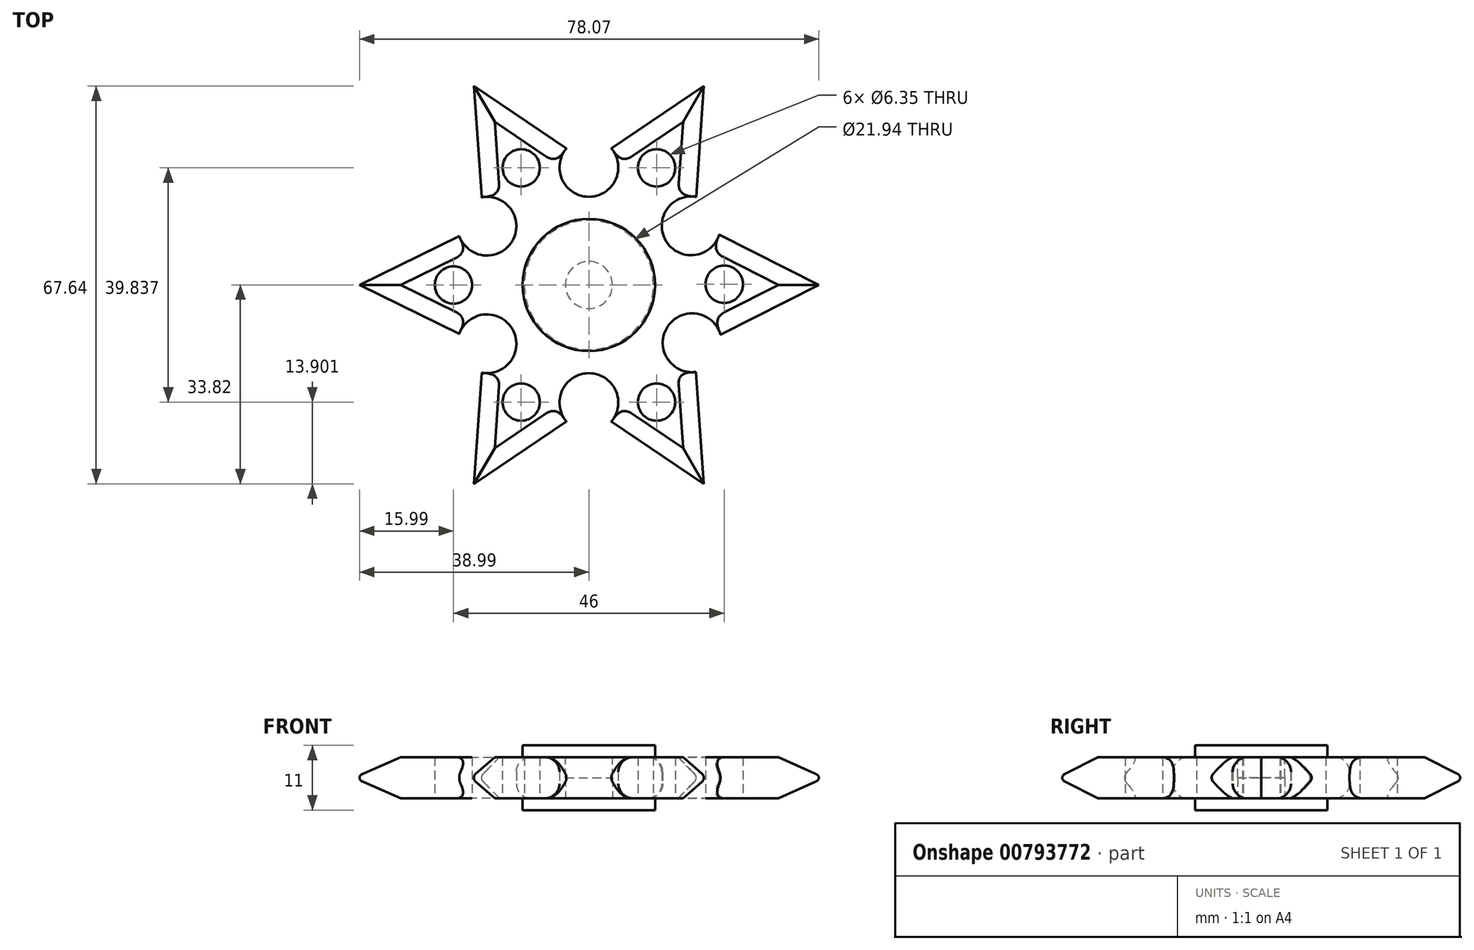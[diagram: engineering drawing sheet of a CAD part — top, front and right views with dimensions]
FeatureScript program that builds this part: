
annotation { "Feature Type Name" : "Feature", "Feature Type Description" : "" }
export const myFeature = defineFeature(function(context is Context, id is Id, definition is map)
    precondition{}
    {
        {
            var Q0;
            Q0=qCreatedBy(makeId("Top.planeOp"),FACE);
            var sketch = newSketch(context, id + "F0", { "sketchPlane" : qUnion([Q0])});
            skCircle(sketch, "E0", {"center": v(0, 0) * mm, "radius": 10.97 * mm});
            skCircle(sketch, "E1.cCircle", {"center": v(0, 0) * mm, "radius": 10.97 * mm, "construction": true});
            skLineSegment(sketch, "E1.0", {"start": v(0, -10.97) * mm, "end": v(-9.5, -5.48) * mm});
            skLineSegment(sketch, "E1.1", {"start": v(-9.5, -5.49) * mm, "end": v(-9.5, 5.49) * mm});
            skLineSegment(sketch, "E1.2", {"start": v(-9.5, 5.49) * mm, "end": v(0, 10.97) * mm});
            skLineSegment(sketch, "E1.3", {"start": v(0, 10.97) * mm, "end": v(9.5, 5.48) * mm});
            skLineSegment(sketch, "E1.4", {"start": v(9.5, 5.49) * mm, "end": v(9.5, -5.49) * mm});
            skLineSegment(sketch, "E1.5", {"start": v(9.5, -5.49) * mm, "end": v(0, -10.97) * mm});
            skLineSegment(sketch, "E2", {"start": v(-18.61, 14.83) * mm, "end": v(-20, 34.64) * mm});
            skLineSegment(sketch, "E3", {"start": v(-20, 34.64) * mm, "end": v(-3.54, 23.54) * mm});
            skLineSegment(sketch, "E4", {"start": v(-39.94, 0) * mm, "end": v(-22.15, 8.7) * mm});
            skLineSegment(sketch, "E5", {"start": v(3.54, 23.54) * mm, "end": v(20, 34.64) * mm});
            skLineSegment(sketch, "E6", {"start": v(-39.94, 0) * mm, "end": v(-22.15, -8.7) * mm});
            skLineSegment(sketch, "E7", {"start": v(20, 34.64) * mm, "end": v(18.63, 14.9) * mm});
            skLineSegment(sketch, "E8", {"start": v(-20, -34.64) * mm, "end": v(-18.61, -14.83) * mm});
            skLineSegment(sketch, "E9", {"start": v(-20, -34.64) * mm, "end": v(-3.54, -23.54) * mm});
            skLineSegment(sketch, "E10", {"start": v(3.54, -23.54) * mm, "end": v(20, -34.64) * mm});
            skLineSegment(sketch, "E11", {"start": v(22.26, 8.97) * mm, "end": v(40, 0) * mm});
            skLineSegment(sketch, "E12", {"start": v(20, -34.64) * mm, "end": v(18.59, -14.73) * mm});
            skLineSegment(sketch, "E13", {"start": v(40, 0) * mm, "end": v(22.46, -8.84) * mm});
            skArc(sketch, "E14", {"start": v(-22.15, 8.7) * mm, "mid": v(-13, 7.5) * mm, "end": v(-18.61, 14.83) * mm});
            skArc(sketch, "E15", {"start": v(-3.54, 23.54) * mm, "mid": v(0, 15) * mm, "end": v(3.54, 23.54) * mm});
            skArc(sketch, "E16", {"start": v(-18.61, -14.83) * mm, "mid": v(-13, -7.5) * mm, "end": v(-22.15, -8.7) * mm});
            skArc(sketch, "E17", {"start": v(3.54, -23.54) * mm, "mid": v(0, -15) * mm, "end": v(-3.54, -23.54) * mm});
            skArc(sketch, "E18", {"start": v(22.46, -8.84) * mm, "mid": v(13.38, -7.09) * mm, "end": v(18.59, -14.73) * mm});
            skArc(sketch, "E19", {"start": v(18.63, 14.9) * mm, "mid": v(13.11, 7.45) * mm, "end": v(22.26, 8.97) * mm});
            skCircle(sketch, "E20", {"center": v(-11.5, 19.92) * mm, "radius": 3.17 * mm});
            skCircle(sketch, "E21", {"center": v(-23, 0) * mm, "radius": 3.17 * mm});
            skCircle(sketch, "E22", {"center": v(-11.5, -19.92) * mm, "radius": 3.17 * mm});
            skCircle(sketch, "E23", {"center": v(11.5, -19.92) * mm, "radius": 3.17 * mm});
            skCircle(sketch, "E24", {"center": v(23, 0.12) * mm, "radius": 3.17 * mm});
            skCircle(sketch, "E25", {"center": v(11.5, 19.92) * mm, "radius": 3.17 * mm});
            skLineSegment(sketch, "E26", {"start": v(-23, 0) * mm, "end": v(0, 0) * mm});
            skLineSegment(sketch, "E27", {"start": v(0, 0) * mm, "end": v(-11.5, 19.92) * mm});
            skLineSegment(sketch, "E28", {"start": v(0, 0) * mm, "end": v(11.5, 19.92) * mm});
            skLineSegment(sketch, "E29", {"start": v(0, 0) * mm, "end": v(23, 0.12) * mm});
            skLineSegment(sketch, "E30", {"start": v(0, 0) * mm, "end": v(11.5, -19.92) * mm});
            skLineSegment(sketch, "E31", {"start": v(0, 0) * mm, "end": v(-11.5, -19.92) * mm});
            skSolve(sketch);
        }
        {
            var Q0;
            Q0 = qSketchRegion(id + "F0", true);
            extrude(context, id + "F1", {"entities" : qUnion([Q0]), "endBound" : BoundingType.SYMMETRIC, "depth" : 7 * mm, "offsetDistance" : 25 * mm});
        }
        {
            var Q0;
            Q0=makeQuery(id+"F1.opExtrude","CAP_EDGE",EDGE,{"disambiguationData":[OSD([sQuery(id+"F0.wireOp",EDGE,"E4")])],"isStart":true});
            var Q1;
            Q1=makeQuery(id+"F1.opExtrude","CAP_EDGE",EDGE,{"disambiguationData":[OSD([sQuery(id+"F0.wireOp",EDGE,"E6")])],"isStart":true});
            var Q2;
            Q2=makeQuery(id+"F1.opExtrude","CAP_EDGE",EDGE,{"disambiguationData":[OSD([sQuery(id+"F0.wireOp",EDGE,"E2")])],"isStart":true});
            var Q3;
            Q3=makeQuery(id+"F1.opExtrude","CAP_EDGE",EDGE,{"disambiguationData":[OSD([sQuery(id+"F0.wireOp",EDGE,"E3")])],"isStart":true});
            var Q4;
            Q4=makeQuery(id+"F1.opExtrude","CAP_EDGE",EDGE,{"disambiguationData":[OSD([sQuery(id+"F0.wireOp",EDGE,"E5")])],"isStart":true});
            var Q5;
            Q5=makeQuery(id+"F1.opExtrude","CAP_EDGE",EDGE,{"disambiguationData":[OSD([sQuery(id+"F0.wireOp",EDGE,"E7")])],"isStart":true});
            var Q6;
            Q6=makeQuery(id+"F1.opExtrude","CAP_EDGE",EDGE,{"disambiguationData":[OSD([sQuery(id+"F0.wireOp",EDGE,"E11")])],"isStart":true});
            var Q7;
            Q7=makeQuery(id+"F1.opExtrude","CAP_EDGE",EDGE,{"disambiguationData":[OSD([sQuery(id+"F0.wireOp",EDGE,"E13")])],"isStart":true});
            var Q8;
            Q8=makeQuery(id+"F1.opExtrude","CAP_EDGE",EDGE,{"disambiguationData":[OSD([sQuery(id+"F0.wireOp",EDGE,"E8")])],"isStart":true});
            var Q9;
            Q9=makeQuery(id+"F1.opExtrude","CAP_EDGE",EDGE,{"disambiguationData":[OSD([sQuery(id+"F0.wireOp",EDGE,"E9")])],"isStart":true});
            var Q10;
            Q10=makeQuery(id+"F1.opExtrude","CAP_EDGE",EDGE,{"disambiguationData":[OSD([sQuery(id+"F0.wireOp",EDGE,"E10")])],"isStart":true});
            var Q11;
            Q11=makeQuery(id+"F1.opExtrude","CAP_EDGE",EDGE,{"disambiguationData":[OSD([sQuery(id+"F0.wireOp",EDGE,"E12")])],"isStart":true});
            var Q12;
            Q12=makeQuery(id+"F1.opExtrude","CAP_EDGE",EDGE,{"disambiguationData":[OSD([sQuery(id+"F0.wireOp",EDGE,"E3")])],"isStart":false});
            var Q13;
            Q13=makeQuery(id+"F1.opExtrude","CAP_EDGE",EDGE,{"disambiguationData":[OSD([sQuery(id+"F0.wireOp",EDGE,"E2")])],"isStart":false});
            var Q14;
            Q14=makeQuery(id+"F1.opExtrude","CAP_EDGE",EDGE,{"disambiguationData":[OSD([sQuery(id+"F0.wireOp",EDGE,"E5")])],"isStart":false});
            var Q15;
            Q15=makeQuery(id+"F1.opExtrude","CAP_EDGE",EDGE,{"disambiguationData":[OSD([sQuery(id+"F0.wireOp",EDGE,"E7")])],"isStart":false});
            var Q16;
            Q16=makeQuery(id+"F1.opExtrude","CAP_EDGE",EDGE,{"disambiguationData":[OSD([sQuery(id+"F0.wireOp",EDGE,"E11")])],"isStart":false});
            var Q17;
            Q17=makeQuery(id+"F1.opExtrude","CAP_EDGE",EDGE,{"disambiguationData":[OSD([sQuery(id+"F0.wireOp",EDGE,"E13")])],"isStart":false});
            var Q18;
            Q18=makeQuery(id+"F1.opExtrude","CAP_EDGE",EDGE,{"disambiguationData":[OSD([sQuery(id+"F0.wireOp",EDGE,"E6")])],"isStart":false});
            var Q19;
            Q19=makeQuery(id+"F1.opExtrude","CAP_EDGE",EDGE,{"disambiguationData":[OSD([sQuery(id+"F0.wireOp",EDGE,"E4")])],"isStart":false});
            var Q20;
            Q20=makeQuery(id+"F1.opExtrude","CAP_EDGE",EDGE,{"disambiguationData":[OSD([sQuery(id+"F0.wireOp",EDGE,"E8")])],"isStart":false});
            var Q21;
            Q21=makeQuery(id+"F1.opExtrude","CAP_EDGE",EDGE,{"disambiguationData":[OSD([sQuery(id+"F0.wireOp",EDGE,"E9")])],"isStart":false});
            var Q22;
            Q22=makeQuery(id+"F1.opExtrude","CAP_EDGE",EDGE,{"disambiguationData":[OSD([sQuery(id+"F0.wireOp",EDGE,"E10")])],"isStart":false});
            var Q23;
            Q23=makeQuery(id+"F1.opExtrude","CAP_EDGE",EDGE,{"disambiguationData":[OSD([sQuery(id+"F0.wireOp",EDGE,"E12")])],"isStart":false});
            chamfer(context, id + "F2", {"entities" : qUnion([Q0, Q1, Q2, Q3, Q4, Q5, Q6, Q7, Q8, Q9, Q10, Q11, Q12, Q13, Q14, Q15, Q16, Q17, Q18, Q19, Q20, Q21, Q22, Q23]), "width" : 3.5 * mm, "tangentPropagation" : true});
        }
        {
            var Q0;
            Q0=makeQuery(id+"F1.opExtrude","CAP_EDGE",EDGE,{"disambiguationData":[OSD([sQuery(id+"F0.wireOp",EDGE,"E16")])],"isStart":true});
            var Q1;
            Q1=makeQuery(id+"F1.opExtrude","CAP_EDGE",EDGE,{"disambiguationData":[OSD([sQuery(id+"F0.wireOp",EDGE,"E16")])],"isStart":false});
            var Q2;
            Q2=makeQuery(id+"F1.opExtrude","CAP_EDGE",EDGE,{"disambiguationData":[OSD([sQuery(id+"F0.wireOp",EDGE,"E14")])],"isStart":true});
            var Q3;
            Q3=makeQuery(id+"F1.opExtrude","CAP_EDGE",EDGE,{"disambiguationData":[OSD([sQuery(id+"F0.wireOp",EDGE,"E14")])],"isStart":false});
            var Q4;
            Q4=makeQuery(id+"F1.opExtrude","CAP_EDGE",EDGE,{"disambiguationData":[OSD([sQuery(id+"F0.wireOp",EDGE,"E15")])],"isStart":true});
            var Q5;
            Q5=makeQuery(id+"F1.opExtrude","CAP_EDGE",EDGE,{"disambiguationData":[OSD([sQuery(id+"F0.wireOp",EDGE,"E19")])],"isStart":true});
            var Q6;
            Q6=makeQuery(id+"F1.opExtrude","CAP_EDGE",EDGE,{"disambiguationData":[OSD([sQuery(id+"F0.wireOp",EDGE,"E18")])],"isStart":true});
            var Q7;
            Q7=makeQuery(id+"F1.opExtrude","CAP_EDGE",EDGE,{"disambiguationData":[OSD([sQuery(id+"F0.wireOp",EDGE,"E17")])],"isStart":true});
            var Q8;
            Q8=makeQuery(id+"F1.opExtrude","CAP_EDGE",EDGE,{"disambiguationData":[OSD([sQuery(id+"F0.wireOp",EDGE,"E19")])],"isStart":false});
            var Q9;
            Q9=makeQuery(id+"F1.opExtrude","CAP_EDGE",EDGE,{"disambiguationData":[OSD([sQuery(id+"F0.wireOp",EDGE,"E18")])],"isStart":false});
            var Q10;
            Q10=makeQuery(id+"F1.opExtrude","CAP_EDGE",EDGE,{"disambiguationData":[OSD([sQuery(id+"F0.wireOp",EDGE,"E17")])],"isStart":false});
            var Q11;
            Q11=makeQuery(id+"F1.opExtrude","CAP_EDGE",EDGE,{"disambiguationData":[OSD([sQuery(id+"F0.wireOp",EDGE,"E15")])],"isStart":false});
            fillet(context, id + "F3", {"entities" : qUnion([Q0, Q1, Q2, Q3, Q4, Q5, Q6, Q7, Q8, Q9, Q10, Q11]), "radius" : 2.5 * mm, "tangentPropagation" : true, "allowEdgeOverflow" : false});
        }
        {
            var Q0;
            Q0=makeQuery(id+"F1.opExtrude","CAP_FACE",FACE,{"disambiguationData":[OSD([sQuery(id+"F0.wireOp",EDGE,"E0"),sQuery(id+"F0.wireOp",EDGE,"E2"),sQuery(id+"F0.wireOp",EDGE,"E3"),sQuery(id+"F0.wireOp",EDGE,"E4"),sQuery(id+"F0.wireOp",EDGE,"E5"),sQuery(id+"F0.wireOp",EDGE,"E6"),sQuery(id+"F0.wireOp",EDGE,"E7"),sQuery(id+"F0.wireOp",EDGE,"E8"),sQuery(id+"F0.wireOp",EDGE,"E9"),sQuery(id+"F0.wireOp",EDGE,"E10"),sQuery(id+"F0.wireOp",EDGE,"E11"),sQuery(id+"F0.wireOp",EDGE,"E12"),sQuery(id+"F0.wireOp",EDGE,"E13"),sQuery(id+"F0.wireOp",EDGE,"E14"),sQuery(id+"F0.wireOp",EDGE,"E15"),sQuery(id+"F0.wireOp",EDGE,"E16"),sQuery(id+"F0.wireOp",EDGE,"E17"),sQuery(id+"F0.wireOp",EDGE,"E18"),sQuery(id+"F0.wireOp",EDGE,"E19")])],"isStart":true});
            var sketch = newSketch(context, id + "F4", { "sketchPlane" : qUnion([Q0])});
            skCircle(sketch, "E32", {"center": v(0, 0) * mm, "radius": 4 * mm});
            skCircle(sketch, "E33", {"center": v(0, 0) * mm, "radius": 11.25 * mm});
            skSolve(sketch);
        }
        {
            var Q0;
            Q0 = qSketchRegion(id + "F4", true);
            var Q1;
            Q1=makeQuery(id+"F4.imprint","IMPRINT",FACE,{"disambiguationData":[TD([[makeQuery(id+"F4.imprint","IMPRINT",EDGE,{"derivedFrom":sQuery(id+"F4.wireOp",EDGE,"E32")}),1.0]])]});
            extrude(context, id + "F5", {"entities" : qUnion([Q0, Q1]), "depth" : 2 * mm, "offsetDistance" : 25 * mm});
        }
        {
            var Q0;
            Q0=makeQuery(id+"F4.imprint","IMPRINT",FACE,{"disambiguationData":[TD([[makeQuery(id+"F4.imprint","IMPRINT",EDGE,{"derivedFrom":sQuery(id+"F4.wireOp",EDGE,"E32")}),1.0]])]});
            extrude(context, id + "F6", {"entities" : qUnion([Q0]), "operationType" : NewBodyOperationType.ADD, "oppositeDirection" : true, "depth" : 3.5 * mm, "offsetDistance" : 25 * mm});
        }
        {
            var Q0;
            {var subQ0=sQuery(id+"F0.wireOp",EDGE,"E9");Q0=makeQuery(id+"F2.opChamfer","BLEND_EDGE",EDGE,{"blendedFrom":[makeQuery(id+"F1.opExtrude","CAP_EDGE",EDGE,{"disambiguationData":[OSD([subQ0])],"isStart":true}),makeQuery(id+"F1.opExtrude","CAP_EDGE",EDGE,{"disambiguationData":[OSD([subQ0])],"isStart":false})],"blendedInto":[]});}
            var Q1;
            {var subQ0=sQuery(id+"F0.wireOp",EDGE,"E10");Q1=makeQuery(id+"F2.opChamfer","BLEND_EDGE",EDGE,{"blendedFrom":[makeQuery(id+"F1.opExtrude","CAP_EDGE",EDGE,{"disambiguationData":[OSD([subQ0])],"isStart":true}),makeQuery(id+"F1.opExtrude","CAP_EDGE",EDGE,{"disambiguationData":[OSD([subQ0])],"isStart":false})],"blendedInto":[]});}
            var Q2;
            {var subQ0=sQuery(id+"F0.wireOp",EDGE,"E12");Q2=makeQuery(id+"F2.opChamfer","BLEND_EDGE",EDGE,{"blendedFrom":[makeQuery(id+"F1.opExtrude","CAP_EDGE",EDGE,{"disambiguationData":[OSD([subQ0])],"isStart":true}),makeQuery(id+"F1.opExtrude","CAP_EDGE",EDGE,{"disambiguationData":[OSD([subQ0])],"isStart":false})],"blendedInto":[]});}
            var Q3;
            {var subQ0=sQuery(id+"F0.wireOp",EDGE,"E13");Q3=makeQuery(id+"F2.opChamfer","BLEND_EDGE",EDGE,{"blendedFrom":[makeQuery(id+"F1.opExtrude","CAP_EDGE",EDGE,{"disambiguationData":[OSD([subQ0])],"isStart":true}),makeQuery(id+"F1.opExtrude","CAP_EDGE",EDGE,{"disambiguationData":[OSD([subQ0])],"isStart":false})],"blendedInto":[]});}
            var Q4;
            {var subQ0=sQuery(id+"F0.wireOp",EDGE,"E11");Q4=makeQuery(id+"F2.opChamfer","BLEND_EDGE",EDGE,{"blendedFrom":[makeQuery(id+"F1.opExtrude","CAP_EDGE",EDGE,{"disambiguationData":[OSD([subQ0])],"isStart":true}),makeQuery(id+"F1.opExtrude","CAP_EDGE",EDGE,{"disambiguationData":[OSD([subQ0])],"isStart":false})],"blendedInto":[]});}
            var Q5;
            {var subQ0=sQuery(id+"F0.wireOp",EDGE,"E7");Q5=makeQuery(id+"F2.opChamfer","BLEND_EDGE",EDGE,{"blendedFrom":[makeQuery(id+"F1.opExtrude","CAP_EDGE",EDGE,{"disambiguationData":[OSD([subQ0])],"isStart":true}),makeQuery(id+"F1.opExtrude","CAP_EDGE",EDGE,{"disambiguationData":[OSD([subQ0])],"isStart":false})],"blendedInto":[]});}
            var Q6;
            {var subQ0=sQuery(id+"F0.wireOp",EDGE,"E5");Q6=makeQuery(id+"F2.opChamfer","BLEND_EDGE",EDGE,{"blendedFrom":[makeQuery(id+"F1.opExtrude","CAP_EDGE",EDGE,{"disambiguationData":[OSD([subQ0])],"isStart":true}),makeQuery(id+"F1.opExtrude","CAP_EDGE",EDGE,{"disambiguationData":[OSD([subQ0])],"isStart":false})],"blendedInto":[]});}
            var Q7;
            {var subQ0=sQuery(id+"F0.wireOp",EDGE,"E3");Q7=makeQuery(id+"F2.opChamfer","BLEND_EDGE",EDGE,{"blendedFrom":[makeQuery(id+"F1.opExtrude","CAP_EDGE",EDGE,{"disambiguationData":[OSD([subQ0])],"isStart":true}),makeQuery(id+"F1.opExtrude","CAP_EDGE",EDGE,{"disambiguationData":[OSD([subQ0])],"isStart":false})],"blendedInto":[]});}
            var Q8;
            {var subQ0=sQuery(id+"F0.wireOp",EDGE,"E2");Q8=makeQuery(id+"F2.opChamfer","BLEND_EDGE",EDGE,{"blendedFrom":[makeQuery(id+"F1.opExtrude","CAP_EDGE",EDGE,{"disambiguationData":[OSD([subQ0])],"isStart":true}),makeQuery(id+"F1.opExtrude","CAP_EDGE",EDGE,{"disambiguationData":[OSD([subQ0])],"isStart":false})],"blendedInto":[]});}
            var Q9;
            {var subQ0=sQuery(id+"F0.wireOp",EDGE,"E4");Q9=makeQuery(id+"F2.opChamfer","BLEND_EDGE",EDGE,{"blendedFrom":[makeQuery(id+"F1.opExtrude","CAP_EDGE",EDGE,{"disambiguationData":[OSD([subQ0])],"isStart":true}),makeQuery(id+"F1.opExtrude","CAP_EDGE",EDGE,{"disambiguationData":[OSD([subQ0])],"isStart":false})],"blendedInto":[]});}
            var Q10;
            {var subQ0=sQuery(id+"F0.wireOp",EDGE,"E6");Q10=makeQuery(id+"F2.opChamfer","BLEND_EDGE",EDGE,{"blendedFrom":[makeQuery(id+"F1.opExtrude","CAP_EDGE",EDGE,{"disambiguationData":[OSD([subQ0])],"isStart":true}),makeQuery(id+"F1.opExtrude","CAP_EDGE",EDGE,{"disambiguationData":[OSD([subQ0])],"isStart":false})],"blendedInto":[]});}
            var Q11;
            {var subQ0=sQuery(id+"F0.wireOp",EDGE,"E8");Q11=makeQuery(id+"F2.opChamfer","BLEND_EDGE",EDGE,{"blendedFrom":[makeQuery(id+"F1.opExtrude","CAP_EDGE",EDGE,{"disambiguationData":[OSD([subQ0])],"isStart":true}),makeQuery(id+"F1.opExtrude","CAP_EDGE",EDGE,{"disambiguationData":[OSD([subQ0])],"isStart":false})],"blendedInto":[]});}
            fillet(context, id + "F7", {"entities" : qUnion([Q0, Q1, Q2, Q3, Q4, Q5, Q6, Q7, Q8, Q9, Q10, Q11]), "radius" : 1 * mm, "tangentPropagation" : true, "allowEdgeOverflow" : false});
        }
        {
            var Q0;
            Q0=makeQuery(id+"F5.opExtrude","SWEPT_BODY",BODY,{"disambiguationData":[OSD([sQuery(id+"F4.wireOp",EDGE,"E33")])]});
            var Q1;
            Q1=qCreatedBy(makeId("Top.planeOp"),FACE);
            mirror(context, id + "F8", {"entities" : qUnion([Q0]), "mirrorPlane" : qUnion([Q1])});
        }
    });
